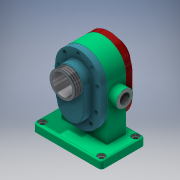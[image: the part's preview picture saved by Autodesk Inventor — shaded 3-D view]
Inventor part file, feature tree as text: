
AUTODESK INVENTOR PART (.ipt)
format: ipt  version: 2018.2 (Build 222227000, 227)  size: 585,216 bytes
history: native  units: in
note: dims shown in document units (in); Inventor stores cm internally (conversion verified against a paired STEP export)
features: sketch x10, extrude x7, hole x5, other x4, plane x3, fillet x2, chamfer x2, mirror x2, imported_body x1, pattern_linear x1, revolve x1, thread x1
ambient origin geometry x8: Origin, YZ Plane, XZ Plane, XY Plane, X Axis, Y Axis, Z Axis, Center Point
bodies: Body1 (feature_tree), Body2 (feature_tree), Body3 (feature_tree)
feature tree (39):
  imported_body  "Base"
  extrude  "Extrusion1"  Depth=4.5276in
  hole  "Hole1"  [1 undecoded]
  pattern_linear  "Rectangular Pattern1"  Count1=2 Spacing1=6.1024in
  plane  "Work Plane1"
  extrude  "Extrusion2"  [1 undecoded]
  revolve  "Revolution1"  [1 undecoded]
  extrude  "Extrusion3"  Depth=1.9685in
  hole  "Hole2"  [1 undecoded]
  hole  "Hole3"  [1 undecoded]
  hole  "Hole4"  [1 undecoded]
  fillet  "Fillet1"  Radius=1.8504in
  chamfer  "Chamfer1"  Distance=1.8504in
  chamfer  "Chamfer2"  Distance=1.9685in Angle=180.0deg
  extrude  "Extrusion4"  Depth=1.9685in TaperAngle=180.0deg
  plane  "Work Plane2"
  mirror  "Mirror1"
  extrude  "Extrusion5"  Depth=0.3937in
  extrude  "Extrusion6"  Depth=0.3937in
  mirror  "Mirror2"
  extrude  "Extrusion7"  Depth=0.0787in
  hole  "Hole7"  [1 undecoded]
  thread  "Thread1"  [1 undecoded]
  plane  "Work Plane3"
  fillet  "Fillet4"  Radius=0.0787in
  sketch  "Sketch1"  dims[d0=7.0866in d1=4.5276in]
  sketch  "Sketch2"  dims[d2=0.7874in d3=0.0in d4=0.4921in]
  sketch  "Sketch3"  dims[d5=0.4921in]
  sketch  "Sketch5"  dims[d6=0.4724in d7=0.2362in d8=0.7087in d9=0.2362in d10=90.0deg d11=0.315in d12=0.8108in d13=0.7874in d15=6.1024in]
  sketch  "Sketch6"  dims[d16=0.7874in d18=3.5433in d19=-1.7717in]
  sketch  "Sketch7"  dims[d20=5.3543in d21=2.3622in]
  sketch  "Sketch8"  dims[d22=1.9685in d23=0.0in d24=0.8661in]
  sketch  "Sketch9"  dims[d25=0.8661in d26=4.0945in]
  other  "Front Cover"
  sketch  "Sketch10"  dims[d27=90.0deg d28=2.3622in]
  sketch  "Sketch11"  dims[d29=1.2795in d30=0.3937in d31=0.0in d32=1.8504in d33=1.8504in d34=1.9685in d36=180.0deg d38=1.9685in d40=180.0deg d42=0.3937in d43=0.2362in d44=0.1575in d45=0.0787in d46=90.0deg d47=0.315in d48=0.8108in d49=0.3937in d50=0.3937in d51=1.0319in d52=2.3622in d53=0.1575in d54=0.0787in d55=90.0deg d56=2.9606in d57=0.8108in d58=0.3937in d59=0.3937in d60=1.0319in d61=2.3622in d62=0.1575in d63=0.0787in d64=90.0deg d65=2.9606in d66=0.8108in d67=0.1575in d68=0.315in d69=0.0787in d70=0.0394in d71=0.0787in d72=45.0deg d73=0.0197in d74=0.0787in d75=45.0deg d76=0.0079in d77=0.0in d78=0.6299in d79=0.0in d80=1.378in d81=0.8661in d82=0.0in d83=0.0787in d84=0.3937in d85=0.3937in d86=1.5748in d87=0.2362in d88=0.1575in d89=0.0787in d90=90.0deg d91=1.1811in d92=0.0in d93=2.5984in d94=0.7874in d95=0.0in d96=0.3937in d97=0.3937in d98=2.126in d99=0.2362in d100=0.1575in d101=0.0787in d102=90.0deg d103=0.315in d104=0.8108in d105=0.3937in d106=0.0in d107=90.0deg d108=0.0787in]
  other  "Pattern of Front Cover:1"
  other  "Back Cover"
  other  "Work Axis1"
note: 8 required parameter values undecoded (feature->parameter linkage not recoverable at this tier; creation-order binding heuristic only, values carry confidence <= 0.55)